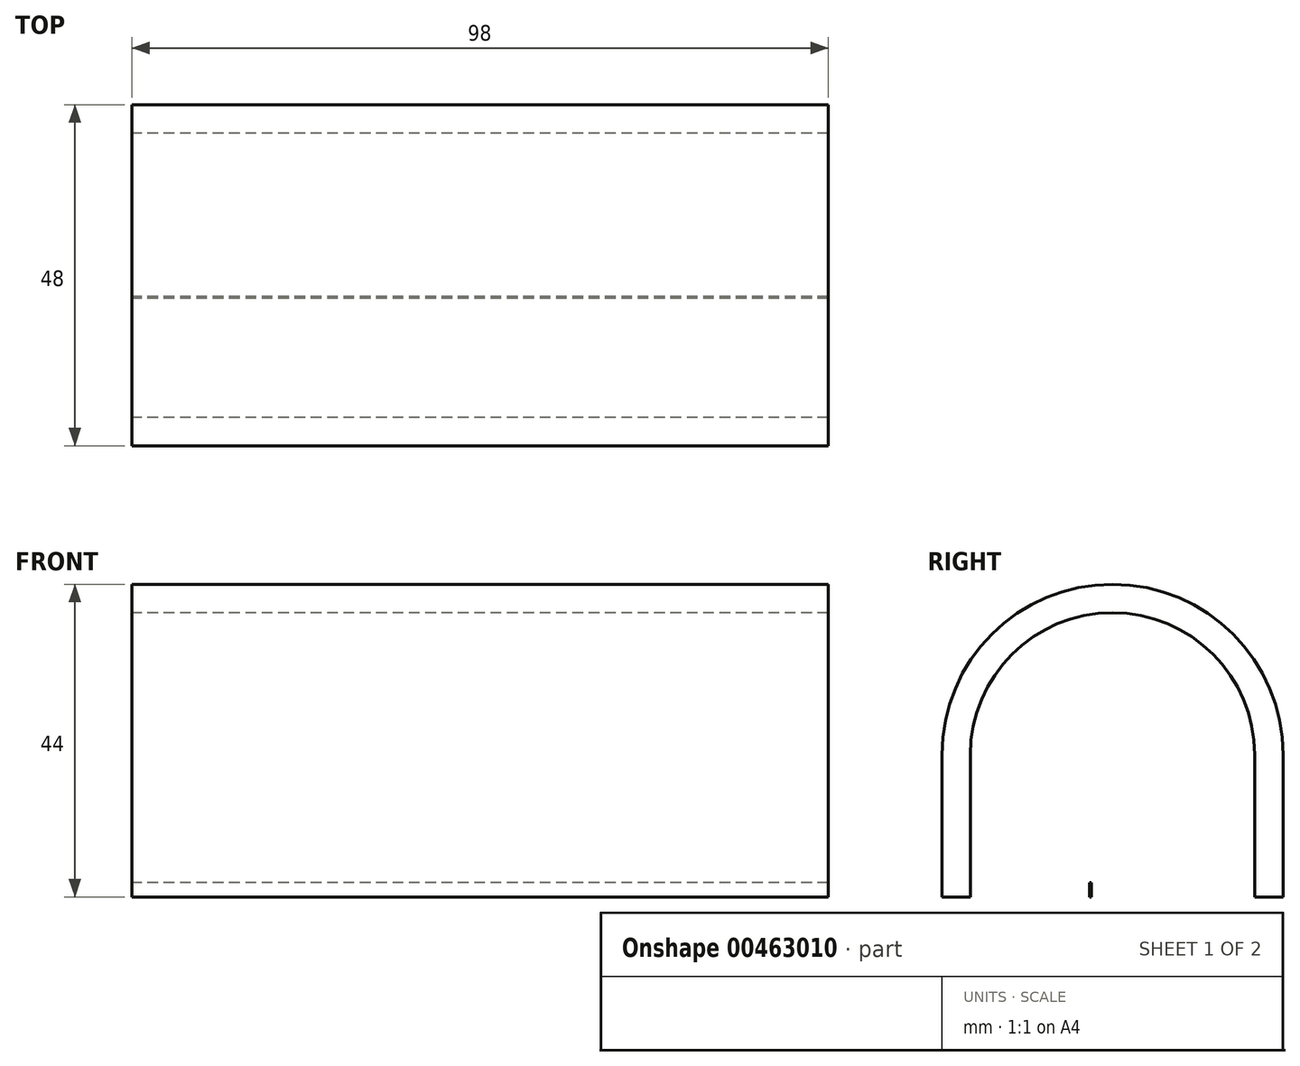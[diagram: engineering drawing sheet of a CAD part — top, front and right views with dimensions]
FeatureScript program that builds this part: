
annotation { "Feature Type Name" : "Feature", "Feature Type Description" : "" }
export const myFeature = defineFeature(function(context is Context, id is Id, definition is map)
    precondition{}
    {
        {
            var Q0;
            Q0=qCreatedBy(makeId("Right.planeOp"),FACE);
            var sketch = newSketch(context, id + "F0", { "sketchPlane" : qUnion([Q0])});
            skLineSegment(sketch, "E0.bottom", {"start": v(-3.25, 0) * mm, "end": v(-3, 0) * mm});
            skLineSegment(sketch, "E0.top", {"start": v(-3.25, 2) * mm, "end": v(-3, 2) * mm});
            skLineSegment(sketch, "E0.left", {"start": v(-3.25, 0) * mm, "end": v(-3.25, 2) * mm});
            skLineSegment(sketch, "E0.right", {"start": v(-3, 0) * mm, "end": v(-3, 2) * mm});
            skSolve(sketch);
        }
        {
            var Q0;
            Q0=qCreatedBy(makeId("Right.planeOp"),FACE);
            var sketch = newSketch(context, id + "F1", { "sketchPlane" : qUnion([Q0])});
            skLineSegment(sketch, "E1.bottom", {"start": v(-20, 0) * mm, "end": v(-24, 0) * mm});
            skLineSegment(sketch, "E1.top", {"start": v(-20, 20) * mm, "end": v(-24, 20) * mm});
            skLineSegment(sketch, "E1.left", {"start": v(-20, 0) * mm, "end": v(-20, 20) * mm});
            skLineSegment(sketch, "E1.right", {"start": v(-24, 0) * mm, "end": v(-24, 20) * mm});
            skLineSegment(sketch, "E2.MirrorCS", {"start": v(20, 0) * mm, "end": v(24, 0) * mm});
            skLineSegment(sketch, "E3.MirrorCS", {"start": v(20, 20) * mm, "end": v(24, 20) * mm});
            skLineSegment(sketch, "E4.MirrorCS", {"start": v(24, 0) * mm, "end": v(24, 20) * mm});
            skLineSegment(sketch, "E5.MirrorCS", {"start": v(20, 0) * mm, "end": v(20, 20) * mm});
            skArc(sketch, "E6", {"start": v(20, 20) * mm, "mid": v(0, 40) * mm, "end": v(-20, 20) * mm});
            skArc(sketch, "E7", {"start": v(24, 20) * mm, "mid": v(0, 44) * mm, "end": v(-24, 20) * mm});
            skSolve(sketch);
        }
        {
            var Q0;
            Q0=makeQuery(id+"F1.imprint","IMPRINT",FACE,{"disambiguationData":[TD([[makeQuery(id+"F1.imprint","IMPRINT",EDGE,{"derivedFrom":sQuery(id+"F1.wireOp",EDGE,"E1.bottom")}),-1.0]])]});
            var Q1;
            Q1=makeQuery(id+"F1.imprint","IMPRINT",FACE,{"disambiguationData":[TD([[makeQuery(id+"F1.imprint","IMPRINT",EDGE,{"derivedFrom":sQuery(id+"F1.wireOp",EDGE,"E2.MirrorCS")}),1.0]])]});
            var Q2;
            Q2=makeQuery(id+"F1.imprint","IMPRINT",FACE,{"disambiguationData":[TD([[makeQuery(id+"F1.imprint","IMPRINT",EDGE,{"derivedFrom":sQuery(id+"F1.wireOp",EDGE,"E1.top")}),-1.0]])]});
            var Q3;
            Q3=makeQuery(id+"F0.imprint","IMPRINT",FACE,{"disambiguationData":[TD([[makeQuery(id+"F0.imprint","IMPRINT",EDGE,{"derivedFrom":sQuery(id+"F0.wireOp",EDGE,"E0.bottom")}),1.0]])]});
            extrude(context, id + "F2", {"entities" : qUnion([Q0, Q1, Q2, Q3]), "depth" : 98 * mm});
        }
    });
